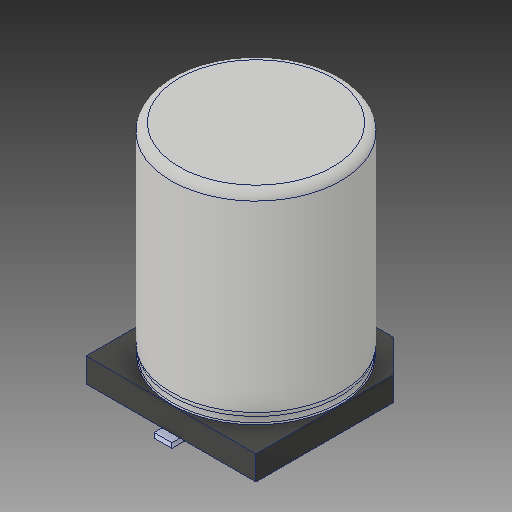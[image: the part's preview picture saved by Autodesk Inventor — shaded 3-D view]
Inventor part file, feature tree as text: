
AUTODESK INVENTOR PART (.ipt)
format: ipt  version: 2018 (Build 220112000, 112)  size: 142,848 bytes
history: native  units: in
note: dims shown in document units (in); Inventor stores cm internally (conversion verified against a paired STEP export)
features: mirror x1
ambient origin geometry x8: Origin, YZ Plane, XZ Plane, XY Plane, X Axis, Y Axis, Z Axis, Center Point
bodies: Solid1 (feature_tree)
feature tree (1):
  mirror  "Mirror1"
